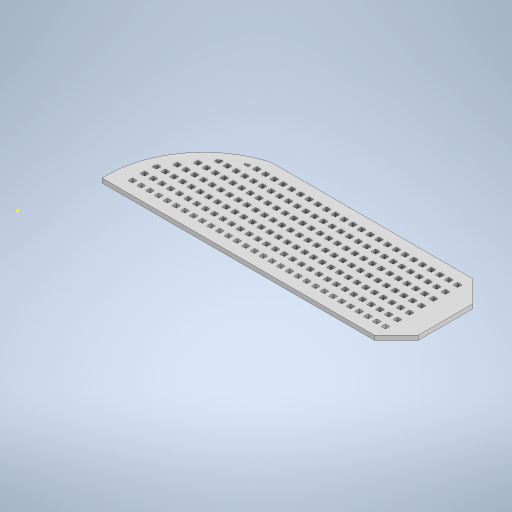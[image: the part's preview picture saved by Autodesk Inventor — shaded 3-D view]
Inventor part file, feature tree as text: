
AUTODESK INVENTOR PART (.ipt)
format: ipt  version: 2024 (Build 280153000, 153)  size: 1,371,136 bytes
history: native  units: mm
features: sketch x6, extrude x4
ambient origin geometry x8: Origin, YZ Plane, XZ Plane, XY Plane, X Axis, Y Axis, Z Axis, Center Point
bodies: Solid1 (feature_tree)
feature tree (10):
  extrude  "Extrusion1"  Depth=2.0mm TaperAngle=0.0deg
  extrude  "Extrusion2"  Depth=3.0mm
  sketch  "Sketch5"  dims[d12=2.0mm d13=1.9mm]
  sketch  "Sketch8"  dims[d14=1.9mm d15=13.0mm]
  extrude  "Extrusion7"  Depth=2.0mm
  extrude  "Extrusion8"  Depth=13.0mm
  sketch  "Sketch1"  dims[d2=2.0mm d3=2.0mm d4=2.0mm d5=2.0mm d6=2.0mm d7=1.5mm d8=2.0mm d9=0.0mm]
  sketch  "Sketch2"  dims[d10=1.9mm d11=3.0mm]
  sketch  "Sketch11"  dims[d16=13.0mm]
  sketch  "Sketch12"  dims[d17=3.0mm d18=3.0mm d19=2.0mm d20=0.0mm d90=2.0mm d91=2.0mm d92=0.0mm d93=2.0mm d94=150.0mm d96=4.0mm d97=120.0mm d99=5.5mm d102=0.0mm d103=5.0mm d104=5.0mm d105=2.0mm d106=2.0mm d109=10.0mm d110=0.0mm d111=2.0mm d112=2.0mm d113=1.0mm d114=70.0mm d116=5.5mm d117=240.0mm d119=4.0mm d122=10.0mm d123=0.0mm d124=2.0mm]
